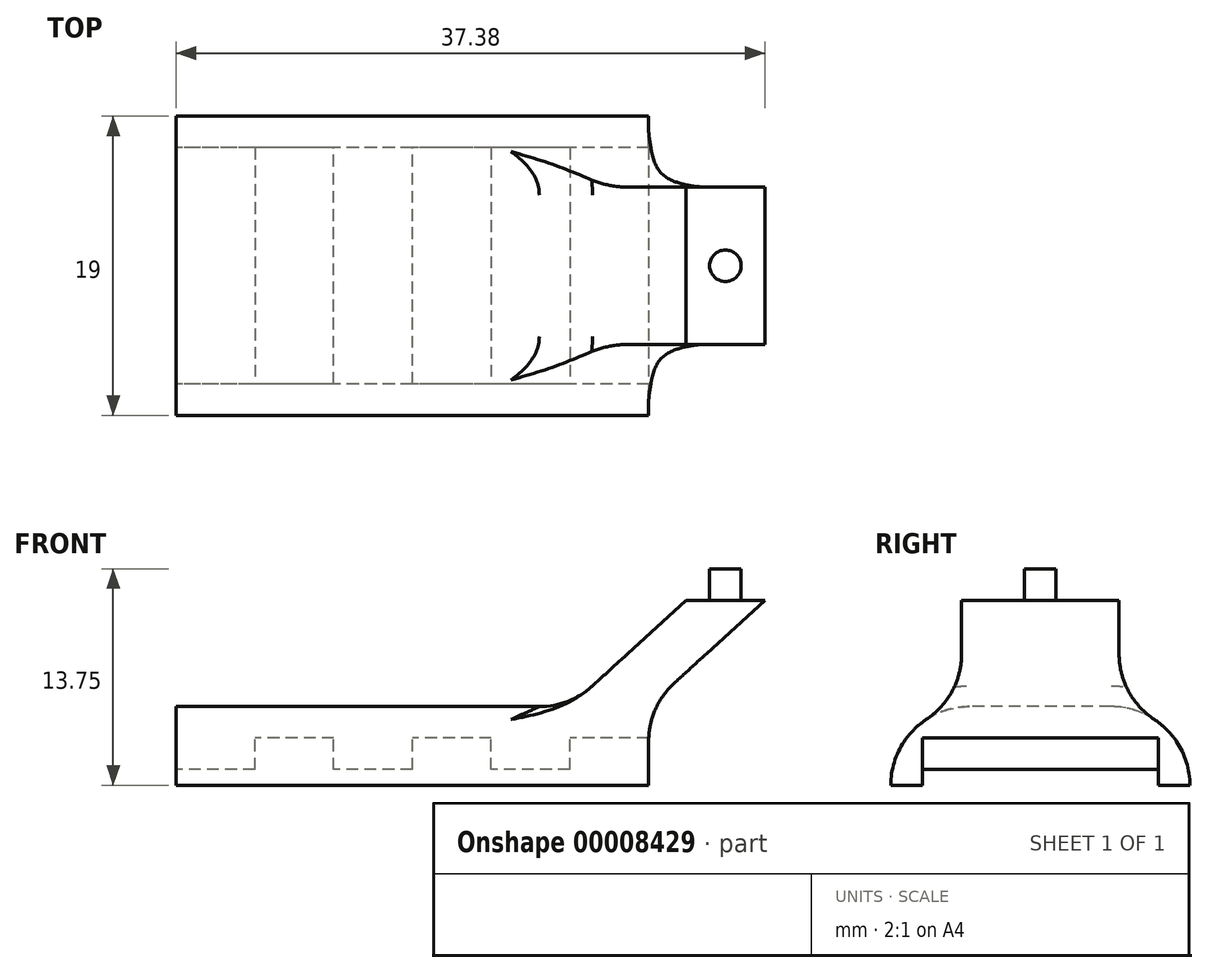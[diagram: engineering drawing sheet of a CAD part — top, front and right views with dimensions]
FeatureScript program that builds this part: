
annotation { "Feature Type Name" : "Feature", "Feature Type Description" : "" }
export const myFeature = defineFeature(function(context is Context, id is Id, definition is map)
    precondition{}
    {
        {
            var Q0;
            Q0=qCreatedBy(makeId("Right.planeOp"),FACE);
            var sketch = newSketch(context, id + "F0", { "sketchPlane" : qUnion([Q0])});
            skLineSegment(sketch, "E0", {"start": v(0, 0) * mm, "end": v(0, 5) * mm});
            skLineSegment(sketch, "E1", {"start": v(0, 5) * mm, "end": v(19, 5) * mm});
            skLineSegment(sketch, "E2", {"start": v(19, 5) * mm, "end": v(19, 0) * mm});
            skLineSegment(sketch, "E3", {"start": v(19, 0) * mm, "end": v(17, 0) * mm});
            skLineSegment(sketch, "E4", {"start": v(17, 0) * mm, "end": v(17, 3) * mm});
            skLineSegment(sketch, "E5", {"start": v(17, 3) * mm, "end": v(2, 3) * mm});
            skLineSegment(sketch, "E6", {"start": v(2, 3) * mm, "end": v(2, 0) * mm});
            skLineSegment(sketch, "E7", {"start": v(2, 0) * mm, "end": v(0, 0) * mm});
            skSolve(sketch);
        }
        {
            var Q0;
            Q0 = qSketchRegion(id + "F0", true);
            extrude(context, id + "F1", {"entities" : qUnion([Q0]), "depth" : 30 * mm});
        }
        {
            var Q0;
            Q0=makeQuery(id+"F1.opExtrude","SWEPT_FACE",FACE,{"disambiguationData":[OSD([sQuery(id+"F0.wireOp",EDGE,"E5")])]});
            var sketch = newSketch(context, id + "F2", { "sketchPlane" : qUnion([Q0])});
            skLineSegment(sketch, "E8.bottom", {"start": v(0, -17) * mm, "end": v(5, -17) * mm});
            skLineSegment(sketch, "E8.top", {"start": v(0, -2) * mm, "end": v(5, -2) * mm});
            skLineSegment(sketch, "E8.left", {"start": v(0, -17) * mm, "end": v(0, -2) * mm});
            skLineSegment(sketch, "E8.right", {"start": v(5, -17) * mm, "end": v(5, -2) * mm});
            skLineSegment(sketch, "E9.bottom", {"start": v(10, -2) * mm, "end": v(15, -2) * mm});
            skLineSegment(sketch, "E9.top", {"start": v(10, -17) * mm, "end": v(15, -17) * mm});
            skLineSegment(sketch, "E9.left", {"start": v(10, -2) * mm, "end": v(10, -17) * mm});
            skLineSegment(sketch, "E9.right", {"start": v(15, -2) * mm, "end": v(15, -17) * mm});
            skLineSegment(sketch, "E10.bottom", {"start": v(20, -17) * mm, "end": v(25, -17) * mm});
            skLineSegment(sketch, "E10.top", {"start": v(20, -2) * mm, "end": v(25, -2) * mm});
            skLineSegment(sketch, "E10.left", {"start": v(20, -17) * mm, "end": v(20, -2) * mm});
            skLineSegment(sketch, "E10.right", {"start": v(25, -17) * mm, "end": v(25, -2) * mm});
            skSolve(sketch);
        }
        {
            var Q0;
            Q0 = qSketchRegion(id + "F2", true);
            extrude(context, id + "F3", {"entities" : qUnion([Q0]), "operationType" : NewBodyOperationType.ADD, "depth" : 2 * mm});
        }
        {
            var Q0;
            Q0=makeQuery(id+"F1.opExtrude","SWEPT_FACE",FACE,{"disambiguationData":[OSD([sQuery(id+"F0.wireOp",EDGE,"E1")])]});
            var sketch = newSketch(context, id + "F4", { "sketchPlane" : qUnion([Q0])});
            skLineSegment(sketch, "E11.bottom", {"start": v(30, 4.5) * mm, "end": v(25, 4.5) * mm});
            skLineSegment(sketch, "E11.top", {"start": v(30, 14.5) * mm, "end": v(25, 14.5) * mm});
            skLineSegment(sketch, "E11.left", {"start": v(30, 4.5) * mm, "end": v(30, 14.5) * mm});
            skLineSegment(sketch, "E11.right", {"start": v(25, 4.5) * mm, "end": v(25, 14.5) * mm});
            skSolve(sketch);
        }
        {
            var Q0;
            Q0=qCreatedBy(makeId("Front.planeOp"),FACE);
            var sketch = newSketch(context, id + "F5", { "sketchPlane" : qUnion([Q0])});
            skLineSegment(sketch, "E12", {"start": v(27.58, 5) * mm, "end": v(34.96, 11.75) * mm});
            skSolve(sketch);
        }
        {
            var Q0;
            Q0=makeQuery(id+"F4.imprint","IMPRINT",FACE,{"disambiguationData":[TD([[makeQuery(id+"F4.imprint","IMPRINT",EDGE,{"derivedFrom":sQuery(id+"F4.wireOp",EDGE,"E11.bottom")}),-1.0]])]});
            var Q1;
            Q1=sQuery(id+"F5.wireOp",EDGE,"E12");
            sweep(context, id + "F6", {"operationType" : NewBodyOperationType.ADD, "profiles" : qUnion([Q0]), "path" : qUnion([Q1])});
        }
        {
            var Q0;
            Q0=makeQuery(id+"F1.opExtrude","SWEPT_EDGE",EDGE,{"disambiguationData":[OSD([sQuery(id+"F0.wireOp",EDGE,"E0"),sQuery(id+"F0.wireOp",EDGE,"E1")])]});
            var Q1;
            Q1=makeQuery(id+"F1.opExtrude","SWEPT_EDGE",EDGE,{"disambiguationData":[OSD([sQuery(id+"F0.wireOp",EDGE,"E1"),sQuery(id+"F0.wireOp",EDGE,"E2")])]});
            fillet(context, id + "F7", {"entities" : qUnion([Q0, Q1]), "radius" : 5 * mm, "tangentPropagation" : true, "allowEdgeOverflow" : false});
        }
        {
            var Q0;
            Q0=makeQuery(id+"F6.opSweep","CAP_EDGE",EDGE,{"disambiguationData":[OSD([sQuery(id+"F4.wireOp",EDGE,"E11.right"),sQuery(id+"F5.wireOp",VERTEX,"E12.start")])],"isStart":true});
            var Q1;
            Q1=makeQuery(id+"F7.opFillet","BLEND_EDGE",EDGE,{"blendedFrom":[makeQuery(id+"F1.opExtrude","SWEPT_EDGE",EDGE,{"disambiguationData":[OSD([sQuery(id+"F0.wireOp",EDGE,"E0"),sQuery(id+"F0.wireOp",EDGE,"E1")])]}),makeQuery(id+"F6.opSweep","SWEPT_FACE",FACE,{"disambiguationData":[OSD([sQuery(id+"F4.wireOp",EDGE,"E11.right"),sQuery(id+"F5.wireOp",EDGE,"E12")])]})],"blendedInto":[makeQuery(id+"F6.opSweep","SWEPT_FACE",FACE,{"disambiguationData":[OSD([sQuery(id+"F4.wireOp",EDGE,"E11.right"),sQuery(id+"F5.wireOp",EDGE,"E12")])]})]});
            var Q2;
            Q2=makeQuery(id+"F7.opFillet","BLEND_EDGE",EDGE,{"blendedFrom":[makeQuery(id+"F1.opExtrude","SWEPT_EDGE",EDGE,{"disambiguationData":[OSD([sQuery(id+"F0.wireOp",EDGE,"E0"),sQuery(id+"F0.wireOp",EDGE,"E1")])]}),makeQuery(id+"F6.opSweep","SWEPT_FACE",FACE,{"disambiguationData":[OSD([sQuery(id+"F4.wireOp",EDGE,"E11.bottom"),sQuery(id+"F5.wireOp",EDGE,"E12")])]})],"blendedInto":[makeQuery(id+"F6.opSweep","SWEPT_FACE",FACE,{"disambiguationData":[OSD([sQuery(id+"F4.wireOp",EDGE,"E11.bottom"),sQuery(id+"F5.wireOp",EDGE,"E12")])]})]});
            var Q3;
            Q3=makeQuery(id+"F7.opFillet","BLEND_EDGE",EDGE,{"blendedFrom":[makeQuery(id+"F1.opExtrude","SWEPT_EDGE",EDGE,{"disambiguationData":[OSD([sQuery(id+"F0.wireOp",EDGE,"E1"),sQuery(id+"F0.wireOp",EDGE,"E2")])]}),makeQuery(id+"F6.opSweep","SWEPT_FACE",FACE,{"disambiguationData":[OSD([sQuery(id+"F4.wireOp",EDGE,"E11.top"),sQuery(id+"F5.wireOp",EDGE,"E12")])]})],"blendedInto":[makeQuery(id+"F6.opSweep","SWEPT_FACE",FACE,{"disambiguationData":[OSD([sQuery(id+"F4.wireOp",EDGE,"E11.top"),sQuery(id+"F5.wireOp",EDGE,"E12")])]})]});
            fillet(context, id + "F8", {"entities" : qUnion([Q0, Q1, Q2, Q3]), "radius" : 5 * mm, "tangentPropagation" : true, "allowEdgeOverflow" : false});
        }
        {
            var Q0;
            Q0=makeQuery(id+"F6.boolean.opBoolean","MERGE",EDGE,{"derivedFrom":[makeQuery(id+"F1.opExtrude","CAP_EDGE",EDGE,{"disambiguationData":[OSD([sQuery(id+"F0.wireOp",EDGE,"E1")])],"isStart":false}),makeQuery(id+"F6.opSweep","CAP_EDGE",EDGE,{"disambiguationData":[OSD([sQuery(id+"F4.wireOp",EDGE,"E11.left"),sQuery(id+"F5.wireOp",VERTEX,"E12.start")])],"isStart":true})]});
            fillet(context, id + "F9", {"entities" : qUnion([Q0]), "radius" : 5 * mm, "tangentPropagation" : true, "allowEdgeOverflow" : false});
        }
        {
            var Q0;
            Q0=makeQuery(id+"F6.opSweep","CAP_FACE",FACE,{"disambiguationData":[OSD([sQuery(id+"F4.wireOp",EDGE,"E11.bottom"),sQuery(id+"F4.wireOp",EDGE,"E11.top"),sQuery(id+"F4.wireOp",EDGE,"E11.left"),sQuery(id+"F4.wireOp",EDGE,"E11.right"),sQuery(id+"F5.wireOp",VERTEX,"E12.end")])],"isStart":false});
            var sketch = newSketch(context, id + "F10", { "sketchPlane" : qUnion([Q0])});
            skCircle(sketch, "E13", {"center": v(34.88, 9.5) * mm, "radius": 1 * mm});
            skSolve(sketch);
        }
        {
            var Q0;
            Q0 = qSketchRegion(id + "F10", true);
            extrude(context, id + "F11", {"entities" : qUnion([Q0]), "operationType" : NewBodyOperationType.ADD, "depth" : 2 * mm});
        }
    });
